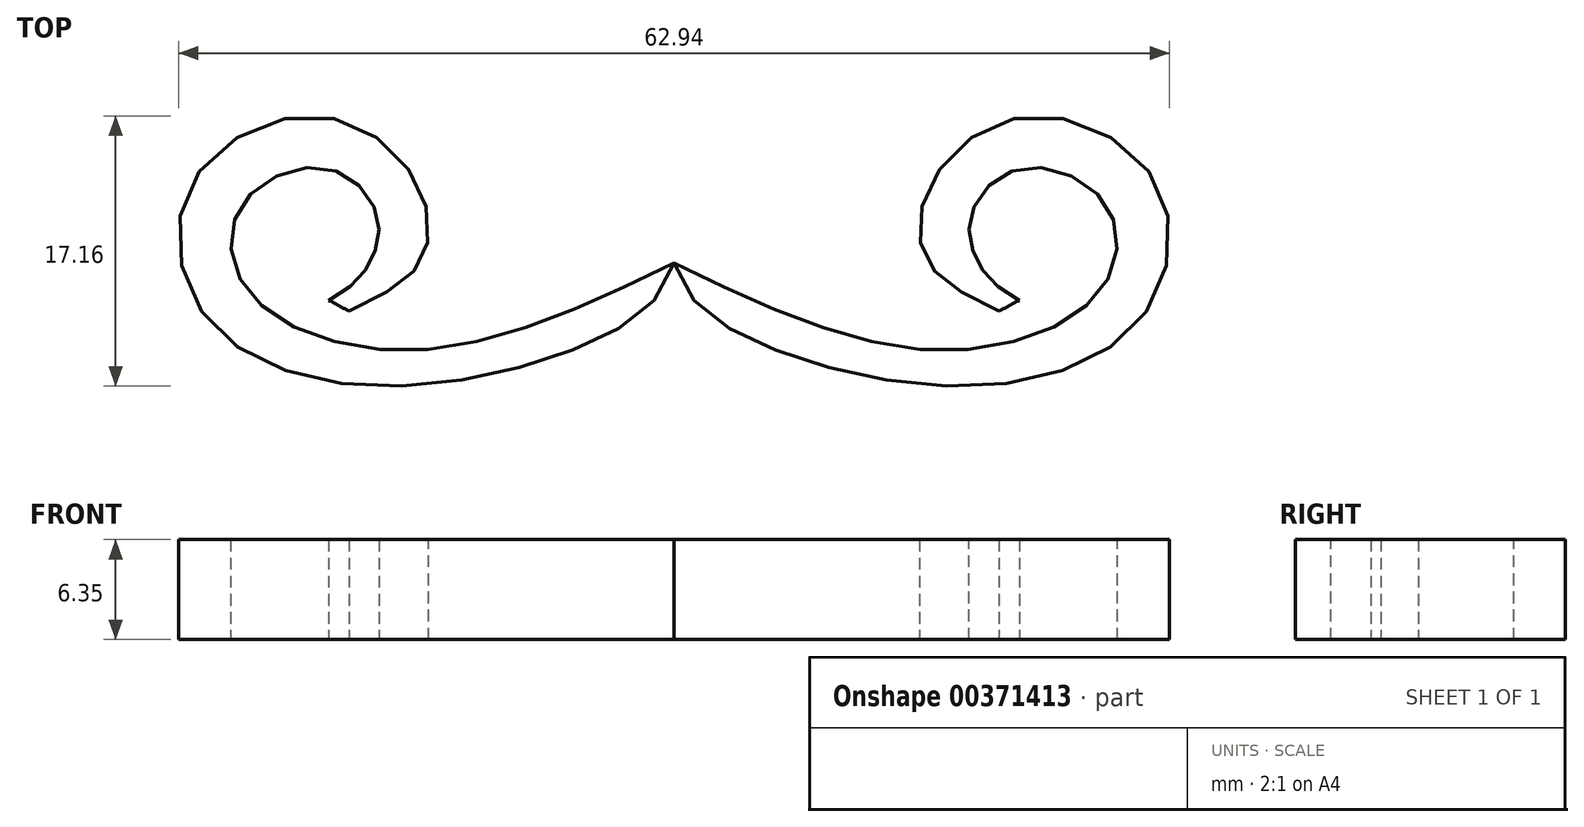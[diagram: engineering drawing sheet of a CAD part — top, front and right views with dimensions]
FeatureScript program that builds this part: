
annotation { "Feature Type Name" : "Feature", "Feature Type Description" : "" }
export const myFeature = defineFeature(function(context is Context, id is Id, definition is map)
    precondition{}
    {
        {
            var Q0;
            Q0=qCreatedBy(makeId("Top.planeOp"),FACE);
            var sketch = newSketch(context, id + "F0", { "sketchPlane" : qUnion([Q0])});
            skFitSpline(sketch, "E0", {"points": [v(0, 0) * mm, v(16.78, -5.54) * mm, v(27.16, -1.66) * mm, v(27.33, 3.87) * mm, v(21.97, 5.99) * mm, v(18.87, 3.06) * mm, v(19.35, 0) * mm, v(21.93, -2.37) * mm], "startDerivative": vector(73.15, -35.05) * mm, "endDerivative": vector(37.13, -18.23) * mm});
            skFitSpline(sketch, "E1", {"points": [v(0, 0) * mm, v(5.72, -5.21) * mm, v(18.9, -7.8) * mm, v(29.59, -3.64) * mm, v(30.6, 5.15) * mm, v(22.25, 9.3) * mm, v(16.15, 4.72) * mm, v(16.15, 0) * mm, v(20.64, -3.03) * mm], "startDerivative": vector(15.84, -64.07) * mm, "endDerivative": vector(61.32, -28.83) * mm});
            skFitSpline(sketch, "E2", {"points": [v(20.64, -3.03) * mm, v(21.93, -2.37) * mm], "startDerivative": vector(1.37, 0.56) * mm, "endDerivative": vector(1.37, 0.56) * mm});
            skFitSpline(sketch, "E3.MirrorCS", {"points": [v(-20.64, -3.03) * mm, v(-21.93, -2.37) * mm], "startDerivative": vector(-1.37, 0.56) * mm, "endDerivative": vector(-1.37, 0.56) * mm});
            skFitSpline(sketch, "E4.MirrorCS", {"points": [v(0, 0) * mm, v(-16.78, -5.54) * mm, v(-27.16, -1.66) * mm, v(-27.33, 3.87) * mm, v(-21.97, 5.99) * mm, v(-18.87, 3.06) * mm, v(-19.35, 0) * mm, v(-21.93, -2.37) * mm], "startDerivative": vector(-73.15, -35.05) * mm, "endDerivative": vector(-37.13, -18.23) * mm});
            skFitSpline(sketch, "E5.MirrorCS", {"points": [v(0, 0) * mm, v(-5.72, -5.21) * mm, v(-18.9, -7.8) * mm, v(-29.59, -3.64) * mm, v(-30.6, 5.15) * mm, v(-22.25, 9.3) * mm, v(-16.15, 4.72) * mm, v(-16.15, 0) * mm, v(-20.64, -3.03) * mm], "startDerivative": vector(-15.84, -64.07) * mm, "endDerivative": vector(-61.32, -28.83) * mm});
            skSolve(sketch);
        }
        {
            var Q0;
            Q0=makeQuery(id+"F0.imprint","IMPRINT",FACE,{"disambiguationData":[TD([[makeQuery(id+"F0.imprint","IMPRINT",EDGE,{"derivedFrom":sQuery(id+"F0.wireOp",EDGE,"E0")}),-1.0]])]});
            var Q1;
            Q1=makeQuery(id+"F0.imprint","IMPRINT",FACE,{"disambiguationData":[TD([[makeQuery(id+"F0.imprint","IMPRINT",EDGE,{"derivedFrom":sQuery(id+"F0.wireOp",EDGE,"E3.MirrorCS")}),-1.0]])]});
            extrude(context, id + "F1", {"entities" : qUnion([Q0, Q1]), "depth" : 6.35 * mm});
        }
    });
